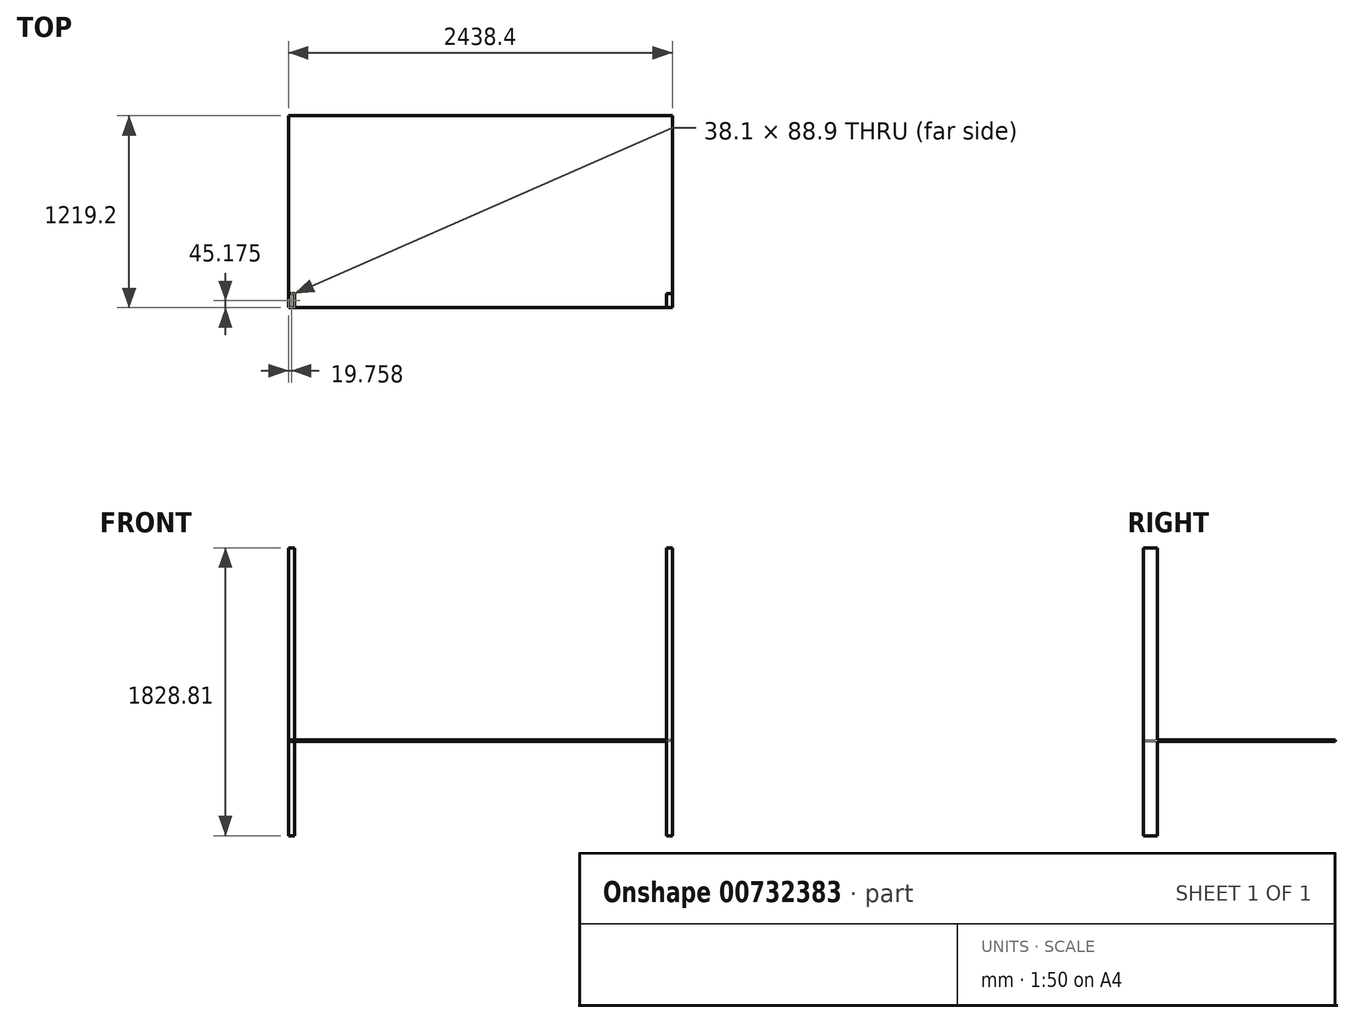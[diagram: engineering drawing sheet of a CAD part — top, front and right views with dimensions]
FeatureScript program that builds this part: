
annotation { "Feature Type Name" : "Feature", "Feature Type Description" : "" }
export const myFeature = defineFeature(function(context is Context, id is Id, definition is map)
    precondition{}
    {
        {
            var Q0;
            Q0=qCreatedBy(makeId("Top.planeOp"),FACE);
            var sketch = newSketch(context, id + "F0", { "sketchPlane" : qUnion([Q0])});
            skLineSegment(sketch, "E0.bottom", {"start": v(-2473.26, 1170.2) * mm, "end": v(-34.86, 1170.2) * mm});
            skLineSegment(sketch, "E0.top", {"start": v(-2473.26, -49) * mm, "end": v(-34.86, -49) * mm});
            skLineSegment(sketch, "E0.left", {"start": v(-2473.26, 1170.2) * mm, "end": v(-2473.26, -49) * mm});
            skLineSegment(sketch, "E0.right", {"start": v(-34.86, 1170.2) * mm, "end": v(-34.86, -49) * mm});
            skSolve(sketch);
        }
        {
            var Q0;
            Q0=makeQuery(id+"F0.imprint","IMPRINT",FACE,{"disambiguationData":[TD([[makeQuery(id+"F0.imprint","IMPRINT",EDGE,{"derivedFrom":sQuery(id+"F0.wireOp",EDGE,"E0.bottom")}),-1.0]])]});
            extrude(context, id + "F1", {"entities" : qUnion([Q0]), "depth" : 9.52 * mm, "offsetDistance" : 25.4 * mm});
        }
        {
            var Q0;
            Q0=makeQuery(id+"F1.opExtrude","CAP_FACE",FACE,{"disambiguationData":[OSD([sQuery(id+"F0.wireOp",EDGE,"E0.bottom"),sQuery(id+"F0.wireOp",EDGE,"E0.top"),sQuery(id+"F0.wireOp",EDGE,"E0.left"),sQuery(id+"F0.wireOp",EDGE,"E0.right")])],"isStart":false});
            var sketch = newSketch(context, id + "F2", { "sketchPlane" : qUnion([Q0])});
            skLineSegment(sketch, "E1.bottom", {"start": v(-2473.26, 1170.2) * mm, "end": v(-2435.16, 1170.2) * mm});
            skLineSegment(sketch, "E1.top", {"start": v(-2473.26, 1081.3) * mm, "end": v(-2435.16, 1081.3) * mm});
            skLineSegment(sketch, "E1.left", {"start": v(-2473.26, 1170.2) * mm, "end": v(-2473.26, 1081.3) * mm});
            skLineSegment(sketch, "E1.right", {"start": v(-2435.16, 1170.2) * mm, "end": v(-2435.16, 1081.3) * mm});
            skLineSegment(sketch, "E2.0.1.0", {"start": v(-2472.55, 40.63) * mm, "end": v(-2434.45, 40.63) * mm});
            skLineSegment(sketch, "E2.0.1.1", {"start": v(-2434.45, 40.63) * mm, "end": v(-2434.45, -48.27) * mm});
            skLineSegment(sketch, "E2.0.1.2", {"start": v(-2472.55, 40.63) * mm, "end": v(-2472.55, -48.27) * mm});
            skLineSegment(sketch, "E2.0.1.3", {"start": v(-2472.55, -48.27) * mm, "end": v(-2434.45, -48.27) * mm});
            skLineSegment(sketch, "E2.1.0.0", {"start": v(-73.66, 1169.48) * mm, "end": v(-35.56, 1169.48) * mm});
            skLineSegment(sketch, "E2.1.0.1", {"start": v(-35.56, 1169.48) * mm, "end": v(-35.56, 1080.58) * mm});
            skLineSegment(sketch, "E2.1.0.2", {"start": v(-73.66, 1169.48) * mm, "end": v(-73.66, 1080.58) * mm});
            skLineSegment(sketch, "E2.1.0.3", {"start": v(-73.66, 1080.58) * mm, "end": v(-35.56, 1080.58) * mm});
            skLineSegment(sketch, "E2.1.1.0", {"start": v(-72.96, 39.9) * mm, "end": v(-34.86, 39.9) * mm});
            skLineSegment(sketch, "E2.1.1.1", {"start": v(-34.86, 39.9) * mm, "end": v(-34.86, -49) * mm});
            skLineSegment(sketch, "E2.1.1.2", {"start": v(-72.96, 39.9) * mm, "end": v(-72.96, -49) * mm});
            skLineSegment(sketch, "E2.1.1.3", {"start": v(-72.96, -49) * mm, "end": v(-34.86, -49) * mm});
            skLineSegment(sketch, "E2.direction1", {"start": v(-2473.26, 1170.2) * mm, "end": v(-73.66, 1169.48) * mm, "construction": true});
            skLineSegment(sketch, "E2.direction2", {"start": v(-2473.26, 1170.2) * mm, "end": v(-2472.55, 40.63) * mm, "construction": true});
            skSolve(sketch);
        }
        {
            var Q0;
            Q0=makeQuery(id+"F2.imprint","IMPRINT",FACE,{"disambiguationData":[TD([[makeQuery(id+"F2.imprint","IMPRINT",EDGE,{"derivedFrom":sQuery(id+"F2.wireOp",EDGE,"E2.0.1.0")}),-1.0]])]});
            var Q1;
            Q1=makeQuery(id+"F2.imprint","IMPRINT",FACE,{"disambiguationData":[TD([[makeQuery(id+"F2.imprint","IMPRINT",EDGE,{"derivedFrom":sQuery(id+"F2.wireOp",EDGE,"E2.1.1.0")}),-1.0]])]});
            extrude(context, id + "F3", {"entities" : qUnion([Q0, Q1]), "operationType" : NewBodyOperationType.ADD, "depth" : 1219.2 * mm, "offsetDistance" : 25.4 * mm, "hasSecondDirection" : true, "secondDirectionOppositeDirection" : true, "secondDirectionDepth" : 609.6 * mm});
        }
    });
